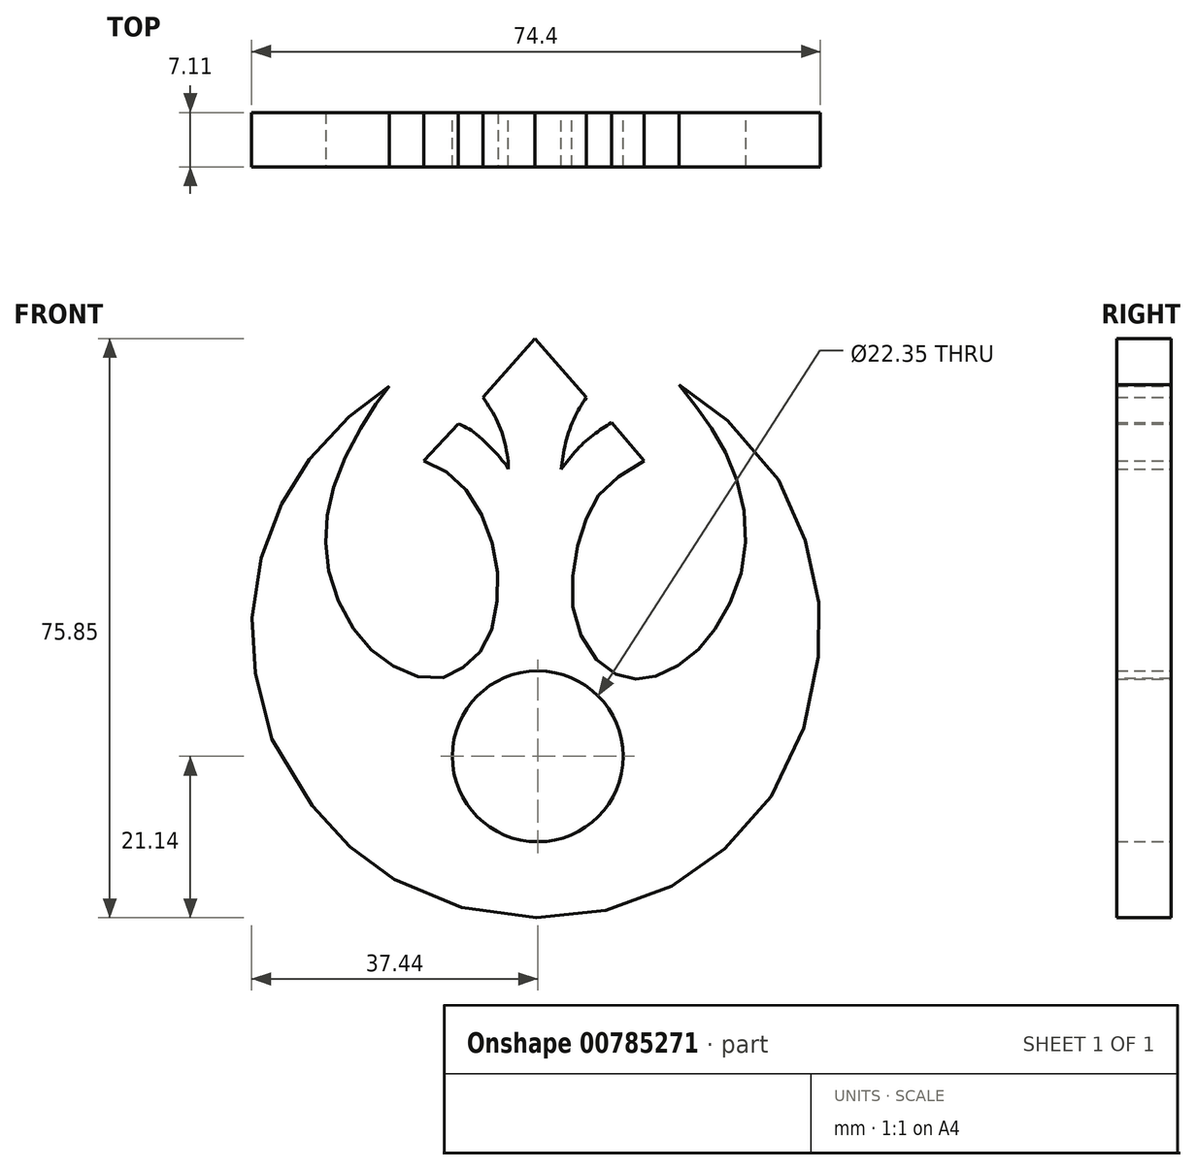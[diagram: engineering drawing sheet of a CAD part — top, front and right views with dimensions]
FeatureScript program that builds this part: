
annotation { "Feature Type Name" : "Feature", "Feature Type Description" : "" }
export const myFeature = defineFeature(function(context is Context, id is Id, definition is map)
    precondition{}
    {
        {
            var Q0;
            Q0=qCreatedBy(makeId("Front.planeOp"),FACE);
            var sketch = newSketch(context, id + "F0", { "sketchPlane" : qUnion([Q0])});
            skFitSpline(sketch, "E0", {"points": [v(-19.44, 48.49) * mm, v(-22.87, 46.04) * mm, v(-27.37, 41.86) * mm, v(-31.04, 37.36) * mm, v(-33.49, 33.06) * mm, v(-35.7, 27.73) * mm, v(-37.2, 20.74) * mm, v(-37.4, 15.06) * mm, v(-36.6, 8.96) * mm, v(-33.77, 0) * mm, v(-27.85, -8.44) * mm, v(-24.54, -11.84) * mm, v(-20.75, -14.83) * mm, v(-12.94, -18.86) * mm, v(-2.49, -21.03) * mm, v(6.4, -20.63) * mm, v(15.36, -18.04) * mm, v(22.06, -14.06) * mm, v(28.1, -8.44) * mm, v(33.46, 0) * mm, v(36.3, 10.1) * mm, v(36.96, 17.2) * mm, v(36.49, 21.9) * mm, v(34.49, 29.87) * mm, v(30.86, 37.18) * mm, v(23.4, 45.2) * mm, v(18.5, 48.65) * mm], "startDerivative": vector(-114.4, -76.16) * mm, "endDerivative": vector(-133.06, 82.7) * mm});
            skFitSpline(sketch, "E1", {"points": [v(18.5, 48.65) * mm, v(22.01, 44) * mm, v(25.07, 38.76) * mm, v(27.06, 31.53) * mm, v(26.6, 23.9) * mm, v(23.4, 17.07) * mm, v(19.91, 12.98) * mm, v(15.56, 10.52) * mm, v(12.44, 10.19) * mm, v(9.09, 11.42) * mm, v(5.52, 16.1) * mm, v(4.51, 23.13) * mm, v(5.96, 30.05) * mm, v(8.53, 34.85) * mm, v(13.93, 38.7) * mm], "startDerivative": vector(50.71, -64.68) * mm, "endDerivative": vector(79.78, 46.78) * mm});
            skFitSpline(sketch, "E2", {"points": [v(-19.44, 48.49) * mm, v(-21.57, 45.53) * mm, v(-24.85, 39.85) * mm, v(-27.2, 33.37) * mm, v(-27.72, 28.3) * mm, v(-26.9, 22.57) * mm, v(-23.9, 16.5) * mm, v(-20.36, 12.78) * mm, v(-15.86, 10.5) * mm, v(-11.76, 10.5) * mm, v(-8.84, 12.39) * mm, v(-6.47, 15.39) * mm, v(-5.29, 20.83) * mm, v(-5.6, 26.43) * mm, v(-7.73, 32.43) * mm, v(-11.05, 36.61) * mm, v(-14.88, 38.7) * mm], "startDerivative": vector(-38.6, -51.52) * mm, "endDerivative": vector(-69.42, 30.3) * mm});
            skLineSegment(sketch, "E3", {"start": v(-14.88, 38.7) * mm, "end": v(-10.42, 43.56) * mm});
            skLineSegment(sketch, "E4", {"start": v(13.93, 38.7) * mm, "end": v(9.65, 43.7) * mm});
            skLineSegment(sketch, "E5", {"start": v(-0.38, 54.7) * mm, "end": v(-7.18, 47.05) * mm});
            skLineSegment(sketch, "E6", {"start": v(-0.38, 54.7) * mm, "end": v(6.39, 47.05) * mm});
            skFitSpline(sketch, "E7", {"points": [v(6.39, 47.05) * mm, v(4.82, 44.38) * mm, v(3.6, 40.83) * mm, v(3.08, 37.6) * mm], "startDerivative": vector(-5.17, -7.87) * mm, "endDerivative": vector(-1.16, -9.66) * mm});
            skFitSpline(sketch, "E8", {"points": [v(3.08, 37.6) * mm, v(5.13, 40.16) * mm, v(7.54, 42.3) * mm, v(9.65, 43.7) * mm], "startDerivative": vector(5.59, 7.56) * mm, "endDerivative": vector(6.8, 4.28) * mm});
            skFitSpline(sketch, "E9", {"points": [v(-10.42, 43.56) * mm, v(-8.09, 42.21) * mm, v(-4.18, 38.2) * mm, v(-3.87, 37.63) * mm], "startDerivative": vector(6.06, -2.55) * mm, "endDerivative": vector(0.95, -2.5) * mm});
            skFitSpline(sketch, "E10", {"points": [v(-7.18, 47.05) * mm, v(-5.52, 44.38) * mm, v(-4.42, 41.46) * mm, v(-3.87, 38.48) * mm, v(-3.87, 37.63) * mm], "startDerivative": vector(6.22, -9.22) * mm, "endDerivative": vector(-0.3, -4.77) * mm});
            skCircle(sketch, "E11", {"center": v(0, 0) * mm, "radius": 11.18 * mm});
            skSolve(sketch);
        }
        {
            var Q0;
            Q0 = qSketchRegion(id + "F0", true);
            extrude(context, id + "F1", {"entities" : qUnion([Q0]), "depth" : 7.11 * mm, "offsetDistance" : 25.4 * mm});
        }
    });
